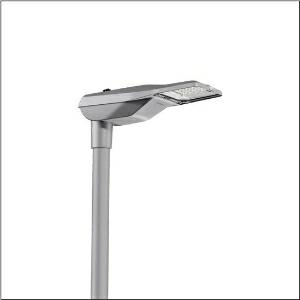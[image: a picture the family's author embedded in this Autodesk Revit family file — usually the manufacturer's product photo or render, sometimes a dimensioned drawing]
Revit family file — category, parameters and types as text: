
# Revit family: streetlight_sl_21_micro___st1_0a_5xe1d33s08db_38a0
name_source: partatom
category: Lighting Fixtures
units: mm (PartAtom-declared; Revit-internal decimal feet)

## family parameters
Cut with Voids When Loaded = No
Host = Face
Light Source = No
Part Type = Normal
Room Calculation Point = No
Round Connector Dimension = Use Diameter
Shared = No

## types (1)
- --- (1 x LED, 5110 lm, 39.1 W, 3000K)
    Apparent Load = 39 VA
    CIE Flux Codes = 37 72 97 100 100
    Color Rendering = 70
    Color Temperature = 3000K
    Default Elevation = 1800 mm
    Description = Streetlight SL 21 micro, mast luminaire, primary light control with lens, of PMMA, primary optical cover: cover, of toughened safety glass, transparent, light distribution: ST1.0a, light emission: direct distribution, primary light characteristic: asymmetric, installation type: side-entry, post-top, LED, High Power LED, rated luminous flux: 5.110lm, luminous efficacy: 131lm/W, light colour: 730, colour temperature: 3000K, control gear: D4i, control: flexible luminous flux parameterisation, time-dependent luminous flux control, constant luminous flux control, overheat protection, pre-setting: logarithmic dimming characteristic, mains connection: 220..240V, AC, 50/60Hz, start of lifetime: 39W, end of service life: 41W, reduction: 18W, luminaire housing, of diecast aluminium, powder-coated, SITECO metallic grey (DB 702S), corrosivity category C5 high according to DIN EN ISO 12944, please order mast flange separately, inclination adjustable: 0°, 5°, 10°, 15°, sealing non-destructively replaceable, multi-level sealing system, length: 528mm, width: 235mm, height: 110mm, mast flange for spigot size: 42mm (side-entry): 5XC10008XM4, 60/48mm (side-entry/post-top): 5XC10108XM2, 76/60mm (side-entry/post-top): 5XC10108XM1, Smart Interface above, protection rating (complete): IP66, insulation class (complete): insulation class II (safety insulation), certification: CE, ENEC, ENEC+, VDE, impact resistance: IK10, permissible operating ambient temperature for outdoor applications: -40..+50°C, standard-compliant lighting for roads and squares, packaging unit: 1 piece

Light Distribution: ST1.0a
    Height = 110 mm
    Lamp = 1 x LED
    Lamp Light Flux = 5110 lm
    Lamp Power = 39.1 W
    Lamp count = 1
    Length = 528 mm
    Luminous efficacy = 131 lm/W
    Manufacturer = Siteco
    ModVariant = No
    Model = 5XE1D33S08DB
    Number of Poles = 1
    OnlyDefault = Yes
    Power Factor = 1
    Product Name = Streetlight SL 21 micro | ST1.0a
    Product group = mast luminaire | pylon top
    ProductGroupID = 6100
    Protection Class = Protection class II
    Protection Degree = IP 66
    RLX_Detail_Level = 1
    RLX_Emergency_Light_Flux = 0 lm
    RLX_Emergency_Type = 0
    RLX_Emergency_Type_DB = No
    RlxData = <blob elided: 98313 chars, md5=94065ef9>
    Socket = socket
    Standby Power = 0 W
    System Light Flux = 5110 lm
    System Power = 39 W
    Type Comments = factory setting: luminous flux: 100 % | dim-lin: 254 | 765 mA
    Type Image = l_1277292.jpg
    URL = http://relux.com
    VarID = @adj_155327
    Voltage = 0 V
    Weight = 0.00 kg
    Width = 235 mm

## geometry (parser evidence)
native form markers: Blend x4, Sweep x9
no freeform markers — native parametric forms only
